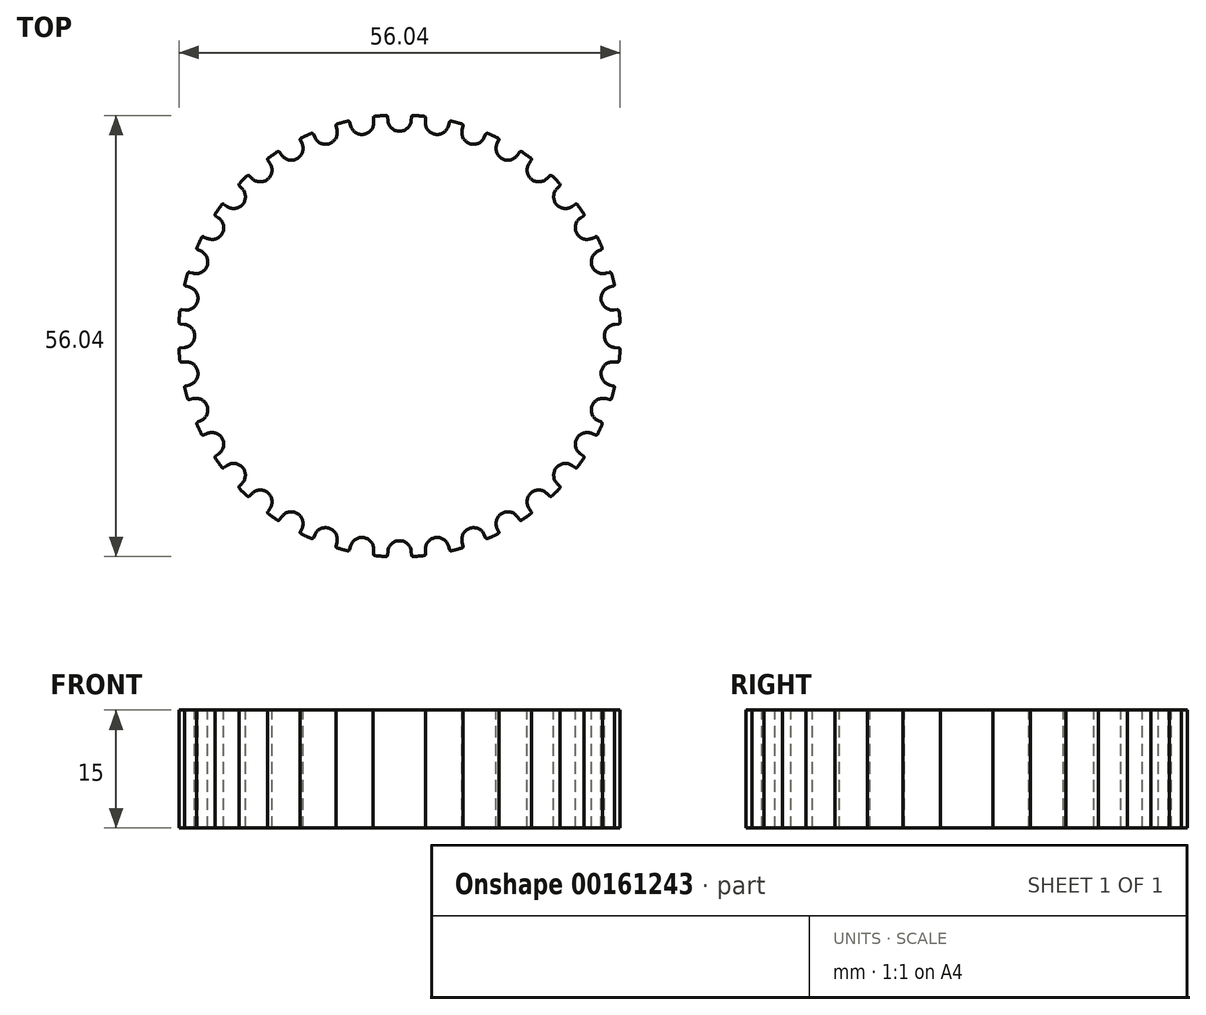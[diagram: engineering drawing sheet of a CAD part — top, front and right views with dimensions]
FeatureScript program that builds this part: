
annotation { "Feature Type Name" : "Feature", "Feature Type Description" : "" }
export const myFeature = defineFeature(function(context is Context, id is Id, definition is map)
    precondition{}
    {
        {
            assignVariable(context, id + "F0", {"name" : "Teeth", "anyValue" : 36});
        }
        {
            assignVariable(context, id + "F1", {"name" : "Width", "anyValue" : 15});
        }
        {
            var Q0;
            Q0=qCreatedBy(makeId("Top.planeOp"),FACE);
            var sketch = newSketch(context, id + "F2", { "sketchPlane" : qUnion([Q0])});
            skCircle(sketch, "E0", {"center": v(0, 0) * mm, "radius": 28.07 * mm});
            skSolve(sketch);
        }
        {
            var Q0;
            Q0=qSketchRegion(id+"F2",true);
            extrude(context, id + "F3", {"entities" : qUnion([Q0]), "depth" : (getVariable(context, 'Width')) * mm});
        }
        {
            var Q0;
            Q0=makeQuery(id+"F3.opExtrude","CAP_FACE",FACE,{"disambiguationData":[OSD([sQuery(id+"F2.wireOp",EDGE,"E0")])],"isStart":false});
            var sketch = newSketch(context, id + "F4", { "sketchPlane" : qUnion([Q0])});
            skCircle(sketch, "E1", {"center": v(0, 0) * mm, "radius": 26.02 * mm, "construction": true});
            skArc(sketch, "E2", {"start": v(-1.48, 27.37) * mm, "mid": v(0, 26.01) * mm, "end": v(1.48, 27.37) * mm});
            skArc(sketch, "E3", {"start": v(1.75, 28.02) * mm, "mid": v(0, 28.08) * mm, "end": v(-1.75, 28.02) * mm});
            skArc(sketch, "E4", {"start": v(-1.53, 27.83) * mm, "mid": v(-1.6, 27.97) * mm, "end": v(-1.75, 28.02) * mm});
            skArc(sketch, "E5", {"start": v(1.75, 28.02) * mm, "mid": v(1.6, 27.97) * mm, "end": v(1.53, 27.83) * mm});
            skLineSegment(sketch, "E6", {"start": v(-1.48, 27.37) * mm, "end": v(-1.53, 27.83) * mm});
            skLineSegment(sketch, "E7", {"start": v(1.53, 27.83) * mm, "end": v(1.48, 27.37) * mm});
            skSolve(sketch);
        }
        {
            var Q0;
            Q0=makeQuery(id+"F4.imprint","IMPRINT",FACE,{"disambiguationData":[TD([[makeQuery(id+"F4.imprint","IMPRINT",EDGE,{"derivedFrom":sQuery(id+"F4.wireOp",EDGE,"E2")}),1.0]])]});
            var Q1;
            Q1=makeQuery(id+"F3.opExtrude","CAP_FACE",FACE,{"disambiguationData":[OSD([sQuery(id+"F2.wireOp",EDGE,"E0")])],"isStart":true});
            extrude(context, id + "F5", {"entities" : qUnion([Q0]), "operationType" : NewBodyOperationType.REMOVE, "endBound" : BoundingType.UP_TO_SURFACE, "oppositeDirection" : true, "endBoundEntityFace" : qUnion([Q1]), "depth" : 25 * mm});
        }
        {
            var Q0;
            Q0=makeQuery(id+"F5.boolean.opBoolean","COPY",FACE,{"derivedFrom":makeQuery(id+"F5.opExtrude","SWEPT_FACE",FACE,{"disambiguationData":[OSD([sQuery(id+"F4.wireOp",EDGE,"E4")])]})});
            var Q1;
            Q1=makeQuery(id+"F5.boolean.opBoolean","COPY",FACE,{"derivedFrom":makeQuery(id+"F5.opExtrude","SWEPT_FACE",FACE,{"disambiguationData":[OSD([sQuery(id+"F4.wireOp",EDGE,"E6")])]})});
            var Q2;
            Q2=makeQuery(id+"F5.boolean.opBoolean","COPY",FACE,{"derivedFrom":makeQuery(id+"F5.opExtrude","SWEPT_FACE",FACE,{"disambiguationData":[OSD([sQuery(id+"F4.wireOp",EDGE,"E2")])]})});
            var Q3;
            Q3=makeQuery(id+"F5.boolean.opBoolean","COPY",FACE,{"derivedFrom":makeQuery(id+"F5.opExtrude","SWEPT_FACE",FACE,{"disambiguationData":[OSD([sQuery(id+"F4.wireOp",EDGE,"E7")])]})});
            var Q4;
            Q4=makeQuery(id+"F5.boolean.opBoolean","COPY",FACE,{"derivedFrom":makeQuery(id+"F5.opExtrude","SWEPT_FACE",FACE,{"disambiguationData":[OSD([sQuery(id+"F4.wireOp",EDGE,"E5")])]})});
            var Q5;
            Q5=makeQuery(id+"F3.opExtrude","SWEPT_FACE",FACE,{"disambiguationData":[OSD([sQuery(id+"F2.wireOp",EDGE,"E0")])]});
            circularPattern(context, id + "F6", {"faces" : qUnion([Q0, Q1, Q2, Q3, Q4]), "axis" : qUnion([Q5]), "angle" : 360 * degree, "instanceCount" : getVariable(context, 'Teeth'), "equalSpace" : true, "patternType" : PatternType.FACE});
        }
    });
